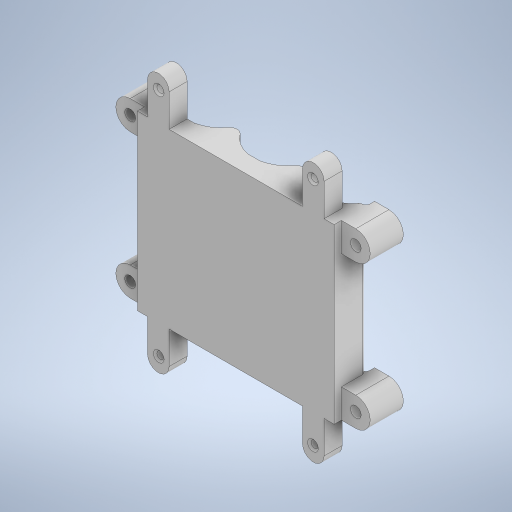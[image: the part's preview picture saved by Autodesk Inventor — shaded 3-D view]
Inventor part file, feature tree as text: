
AUTODESK INVENTOR PART (.ipt)
format: ipt  version: 2023.1 (Build 271208000, 208)  size: 423,424 bytes
history: native  units: mm
features: extrude x5, sketch x5, projected_geometry x5, fillet x4, other x1, chamfer x1
ambient origin geometry x8: Origin, YZ Plane, XZ Plane, XY Plane, X Axis, Y Axis, Z Axis, Center Point
bodies: Body1 (feature_tree)
feature tree (21):
  other  "솔리드1"
  extrude  "돌출1"  Depth=62.6mm
  extrude  "돌출2"  Depth=40.0mm
  fillet  "모깎기1"  Radius=3.0mm
  fillet  "모깎기2"  Radius=3.0mm
  extrude  "돌출3"  Depth=3.0mm
  fillet  "모깎기3"  Radius=3.0mm
  extrude  "돌출4"  Depth=54.6mm
  extrude  "돌출5"  Depth=48.0mm
  fillet  "모깎기4"  Radius=8.0mm
  chamfer  "모따기1"  Distance=5.0mm
  sketch  "스케치1"
  sketch  "스케치2"
  sketch  "스케치3"
  projected_geometry  "투영된 루프1"
  projected_geometry  "투영된 루프2"
  projected_geometry  "투영된 루프3"
  projected_geometry  "투영된 루프4"
  sketch  "스케치5"
  projected_geometry  "투영된 루프5"
  sketch  "스케치6"
